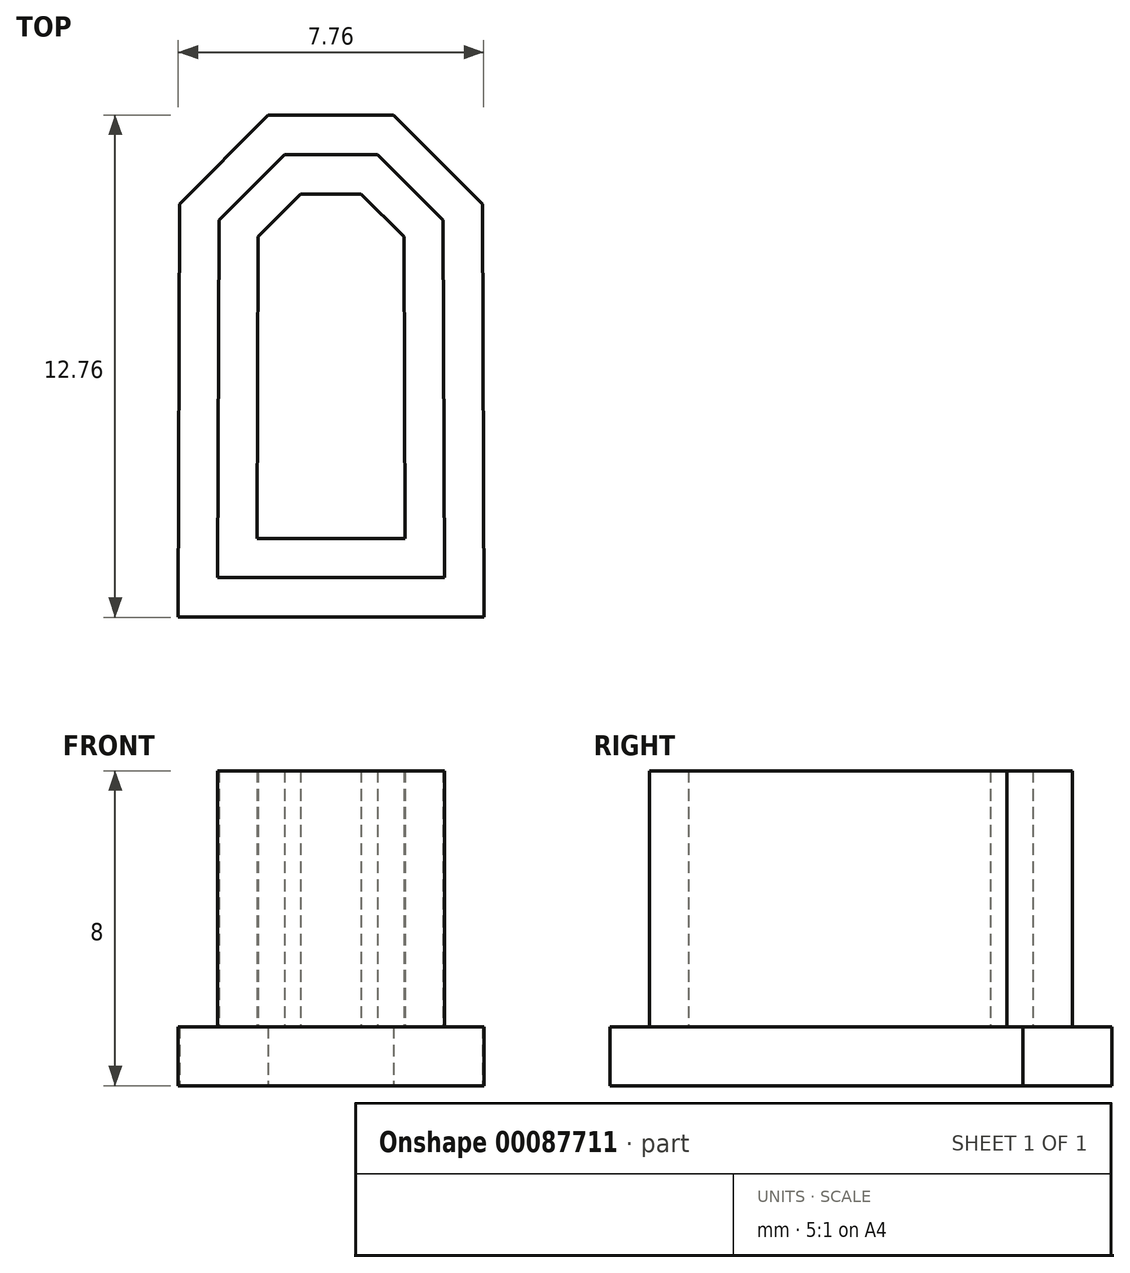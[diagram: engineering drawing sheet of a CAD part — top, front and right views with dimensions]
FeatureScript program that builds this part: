
annotation { "Feature Type Name" : "Feature", "Feature Type Description" : "" }
export const myFeature = defineFeature(function(context is Context, id is Id, definition is map)
    precondition{}
    {
        {
            var Q0;
            Q0=qCreatedBy(makeId("Top.planeOp"),FACE);
            var sketch = newSketch(context, id + "F0", { "sketchPlane" : qUnion([Q0])});
            skLineSegment(sketch, "E0.top", {"start": v(1.88, -4.38) * mm, "end": v(-1.87, -4.38) * mm});
            skPoint(sketch, "E0.middle", {"position": v(0, 0) * mm});
            skCircle(sketch, "E1.cCircle", {"center": v(0, 2.52) * mm, "radius": 1.85 * mm, "construction": true});
            skLineSegment(sketch, "E1.0", {"start": v(-0.77, 4.38) * mm, "end": v(0.77, 4.38) * mm});
            skLineSegment(sketch, "E1.1", {"start": v(0.77, 4.38) * mm, "end": v(1.85, 3.3) * mm});
            skLineSegment(sketch, "E1.2", {"start": v(1.85, 3.3) * mm, "end": v(1.85, 1.76) * mm});
            skLineSegment(sketch, "E1.3", {"start": v(1.85, 1.76) * mm, "end": v(0.77, 0.67) * mm});
            skLineSegment(sketch, "E1.4", {"start": v(0.77, 0.67) * mm, "end": v(-0.77, 0.67) * mm});
            skLineSegment(sketch, "E1.5", {"start": v(-0.77, 0.67) * mm, "end": v(-1.85, 1.76) * mm});
            skLineSegment(sketch, "E1.6", {"start": v(-1.85, 1.76) * mm, "end": v(-1.85, 3.3) * mm});
            skLineSegment(sketch, "E1.7", {"start": v(-1.85, 3.3) * mm, "end": v(-0.77, 4.38) * mm});
            skPoint(sketch, "E1.0.midPoint", {"position": v(0, 4.38) * mm});
            skLineSegment(sketch, "E2", {"start": v(-1.85, 3.3) * mm, "end": v(-1.87, -4.38) * mm});
            skLineSegment(sketch, "E3", {"start": v(1.85, 3.3) * mm, "end": v(1.88, -4.38) * mm});
            skLineSegment(sketch, "E4.0", {"start": v(-2.85, 3.7) * mm, "end": v(-1.18, 5.38) * mm});
            skLineSegment(sketch, "E4.1", {"start": v(2.88, -5.38) * mm, "end": v(-2.88, -5.38) * mm});
            skLineSegment(sketch, "E4.2", {"start": v(2.85, 3.7) * mm, "end": v(2.88, -5.38) * mm});
            skLineSegment(sketch, "E4.3", {"start": v(-2.85, 3.7) * mm, "end": v(-2.88, -5.38) * mm});
            skLineSegment(sketch, "E4.4", {"start": v(1.18, 5.38) * mm, "end": v(2.85, 3.7) * mm});
            skLineSegment(sketch, "E4.5", {"start": v(-1.18, 5.38) * mm, "end": v(1.18, 5.38) * mm});
            skLineSegment(sketch, "E5.0", {"start": v(-3.85, 4.12) * mm, "end": v(-1.6, 6.38) * mm});
            skLineSegment(sketch, "E5.1", {"start": v(3.88, -6.38) * mm, "end": v(-3.88, -6.38) * mm});
            skLineSegment(sketch, "E5.2", {"start": v(3.85, 4.12) * mm, "end": v(3.88, -6.38) * mm});
            skLineSegment(sketch, "E5.3", {"start": v(-3.85, 4.12) * mm, "end": v(-3.88, -6.38) * mm});
            skLineSegment(sketch, "E5.4", {"start": v(1.6, 6.38) * mm, "end": v(3.85, 4.12) * mm});
            skLineSegment(sketch, "E5.5", {"start": v(-1.6, 6.38) * mm, "end": v(1.6, 6.38) * mm});
            skSolve(sketch);
        }
        {
            var Q0;
            Q0=makeQuery(id+"F0.imprint","IMPRINT",FACE,{"disambiguationData":[TD([[makeQuery(id+"F0.imprint","IMPRINT",EDGE,{"derivedFrom":sQuery(id+"F0.wireOp",EDGE,"E0.top")}),1.0]])]});
            extrude(context, id + "F1", {"entities" : qUnion([Q0]), "depth" : 8 * mm});
        }
        {
            var Q0;
            Q0=makeQuery(id+"F0.imprint","IMPRINT",FACE,{"disambiguationData":[TD([[makeQuery(id+"F0.imprint","IMPRINT",EDGE,{"derivedFrom":sQuery(id+"F0.wireOp",EDGE,"E4.0")}),1.0]])]});
            var Q1;
            Q1=makeQuery(id+"F0.imprint","IMPRINT",FACE,{"disambiguationData":[TD([[makeQuery(id+"F0.imprint","IMPRINT",EDGE,{"derivedFrom":sQuery(id+"F0.wireOp",EDGE,"E0.top")}),-1.0]])]});
            var Q2;
            Q2=makeQuery(id+"F0.imprint","IMPRINT",FACE,{"disambiguationData":[TD([[makeQuery(id+"F0.imprint","IMPRINT",EDGE,{"derivedFrom":sQuery(id+"F0.wireOp",EDGE,"E1.0")}),-1.0]])]});
            extrude(context, id + "F2", {"entities" : qUnion([Q0, Q1, Q2]), "operationType" : NewBodyOperationType.ADD, "depth" : 1.5 * mm});
        }
    });
